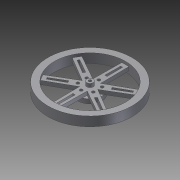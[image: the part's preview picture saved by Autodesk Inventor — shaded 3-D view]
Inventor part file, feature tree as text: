
AUTODESK INVENTOR PART (.ipt)
format: ipt  version: 2011 SP2 (Build 150309200, 309)  size: 222,720 bytes
history: native  units: mm
features: extrude x5, sketch x3
ambient origin geometry x8: Origin, YZ Plane, XZ Plane, XY Plane, X Axis, Y Axis, Z Axis, Center Point
bodies: Solid1 (feature_tree)
feature tree (8):
  sketch  "Sketch1"  dims[d0=90.0mm d1=76.0mm]
  extrude  "Extrusion1"  Depth=76.0mm
  extrude  "Extrusion2"  Depth=2.5mm
  extrude  "Extrusion3"  Depth=1.05mm
  sketch  "Sketch3"  dims[d4=1.25mm d5=1.05mm d6=3.0mm d7=17.0mm d8=4.0mm d9=9.53mm d10=60.0mm d12=360.0deg d14=60.0mm d16=360.0deg d18=10.0mm d19=0.0mm d20=3.207mm d21=4.0mm d22=0.0mm d23=7.0mm d24=3.9mm d25=0.0mm d26=6.0mm d27=11.0mm d28=25.4mm d29=4.6mm d30=0.0mm d31=9.2mm d32=0.0mm]
  extrude  "Extrusion4"  Depth=3.0mm
  extrude  "Extrusion5"  Depth=17.0mm
  sketch  "Sketch2"  dims[d2=2.1mm d3=2.5mm]
